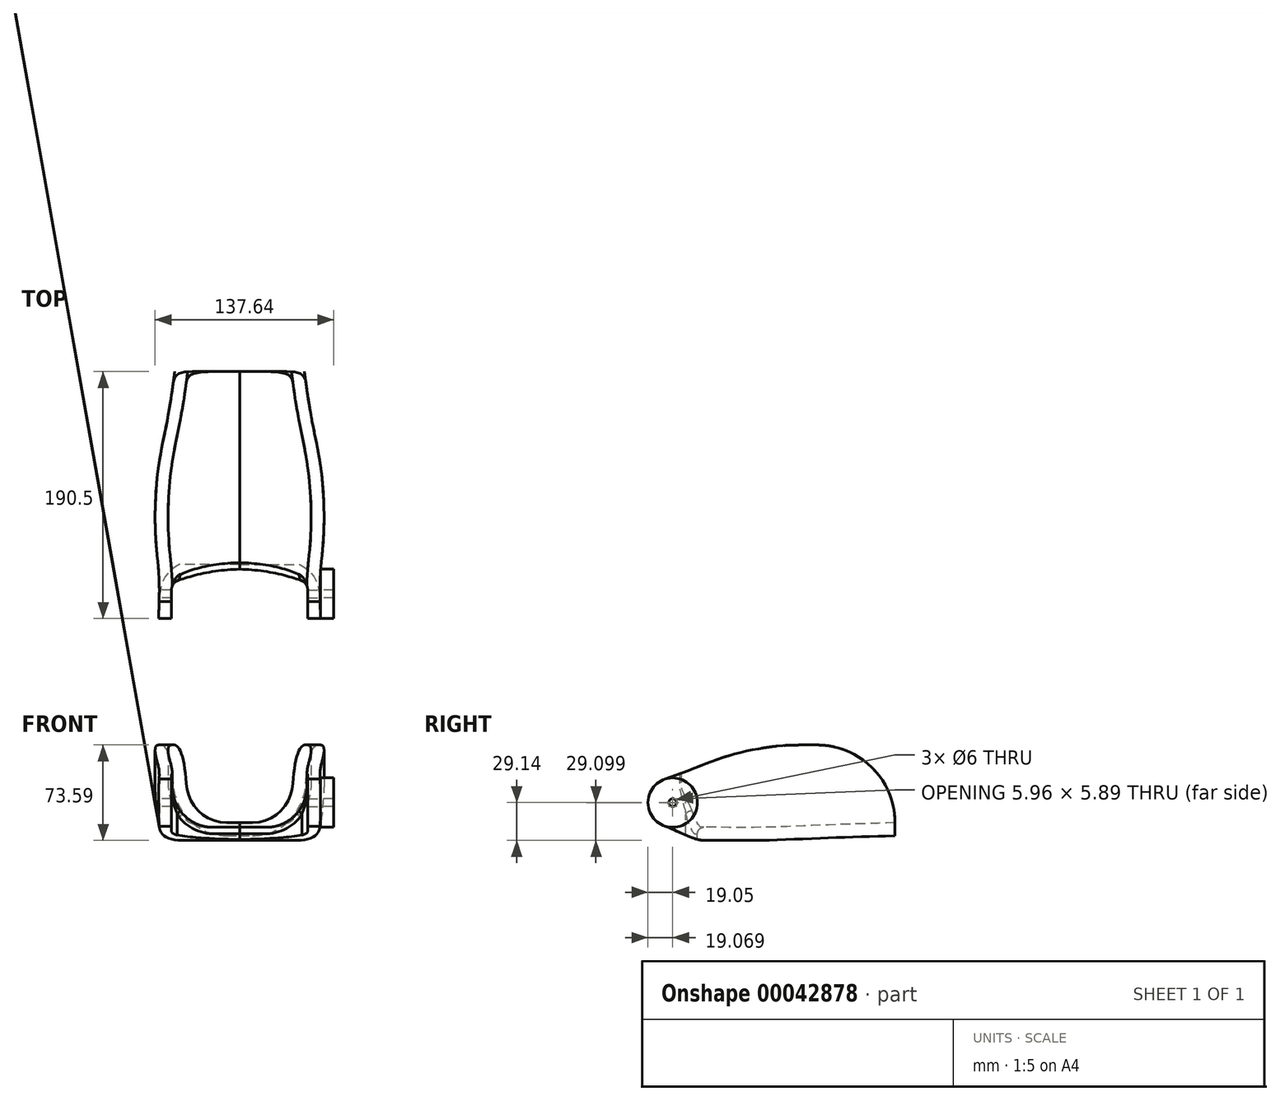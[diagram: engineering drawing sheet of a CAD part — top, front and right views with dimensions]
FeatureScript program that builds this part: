
annotation { "Feature Type Name" : "Feature", "Feature Type Description" : "" }
export const myFeature = defineFeature(function(context is Context, id is Id, definition is map)
    precondition{}
    {
        {
            assignVariable(context, id + "F0", {"name" : "FST", "anyValue" : 10 * mm});
        }
        {
            assignVariable(context, id + "F1", {"name" : "FSG", "anyValue" : 5 * mm});
        }
        {
            var Q0;
            Q0=qCreatedBy(makeId("Right.planeOp"),FACE);
            cPlane(context, id + "F2", {"entities" : qUnion([Q0]), "cplaneType" : CPlaneType.OFFSET, "offset" : (115 * mm / 2) + getVariable(context, 'FSG'), "width" : 150 * mm, "height" : 150 * mm});
        }
        {
            var Q0;
            Q0=qCreatedBy(makeId("Front.planeOp"),FACE);
            cPlane(context, id + "F3", {"entities" : qUnion([Q0]), "cplaneType" : CPlaneType.OFFSET, "offset" : 114.3 * mm, "width" : 150 * mm, "height" : 150 * mm});
        }
        {
            var Q0;
            Q0=qCreatedBy(makeId("Front.planeOp"),FACE);
            cPlane(context, id + "F4", {"entities" : qUnion([Q0]), "cplaneType" : CPlaneType.OFFSET, "offset" : 76.2 * mm, "width" : 150 * mm, "height" : 150 * mm});
        }
        {
            var Q0;
            Q0=qCreatedBy(makeId("Front.planeOp"),FACE);
            cPlane(context, id + "F5", {"entities" : qUnion([Q0]), "cplaneType" : CPlaneType.OFFSET, "offset" : (76.2 * mm) - 15 * mm, "width" : 150 * mm, "height" : 150 * mm});
        }
        {
            var Q0;
            Q0=qCreatedBy(makeId("Front.planeOp"),FACE);
            cPlane(context, id + "F6", {"entities" : qUnion([Q0]), "cplaneType" : CPlaneType.OFFSET, "offset" : (76.2 * mm) - 49 * mm, "width" : 150 * mm, "height" : 150 * mm});
        }
        {
            var Q0;
            Q0=qCreatedBy(makeId("Top.planeOp"),FACE);
            cPlane(context, id + "F7", {"entities" : qUnion([Q0]), "cplaneType" : CPlaneType.OFFSET, "offset" : 63.5 * mm + 10 * mm, "oppositeDirection" : true, "width" : 150 * mm, "height" : 150 * mm});
        }
        {
            var Q0;
            Q0=qCreatedBy(makeId("Front.planeOp"),FACE);
            cPlane(context, id + "F8", {"entities" : qUnion([Q0]), "cplaneType" : CPlaneType.OFFSET, "offset" : 76.2 * mm, "oppositeDirection" : true, "width" : 150 * mm, "height" : 150 * mm});
        }
        {
            var Q0;
            Q0=qCreatedBy(makeId("Front.planeOp"),FACE);
            cPlane(context, id + "F9", {"entities" : qUnion([Q0]), "cplaneType" : CPlaneType.OFFSET, "offset" : 76.2 * mm - 33.4 * mm, "oppositeDirection" : true, "width" : 150 * mm, "height" : 150 * mm});
        }
        {
            var Q0;
            Q0=qCreatedBy(makeId("Front.planeOp"),FACE);
            cPlane(context, id + "F10", {"entities" : qUnion([Q0]), "cplaneType" : CPlaneType.OFFSET, "offset" : 76.2 * mm - 73.4 * mm, "oppositeDirection" : true, "width" : 150 * mm, "height" : 150 * mm});
        }
        {
            var Q0;
            Q0=qCreatedBy(makeId("Top.planeOp"),FACE);
            var sketch = newSketch(context, id + "F11", { "sketchPlane" : qUnion([Q0])});
            skLineSegment(sketch, "E0", {"start": v(0, 76.2) * mm, "end": v(0, -76.2) * mm, "construction": true});
            skPoint(sketch, "E1", {"position": v(0, 0) * mm});
            skLineSegment(sketch, "E2", {"start": v(0, -76.2) * mm, "end": v(52.5, -76.2) * mm, "construction": true});
            skLineSegment(sketch, "E3", {"start": v(0, -61.2) * mm, "end": v(54, -61.2) * mm, "construction": true});
            skLineSegment(sketch, "E4", {"start": v(0, -27.2) * mm, "end": v(55, -27.2) * mm, "construction": true});
            skLineSegment(sketch, "E5", {"start": v(0, 2.8) * mm, "end": v(52.5, 2.8) * mm, "construction": true});
            skLineSegment(sketch, "E6", {"start": v(0, 42.8) * mm, "end": v(45, 42.8) * mm, "construction": true});
            skLineSegment(sketch, "E7", {"start": v(0, 76.2) * mm, "end": v(40, 76.2) * mm, "construction": true});
            skLineSegment(sketch, "E8.bottom", {"start": v(-157.02, 34.24) * mm, "end": v(-106.22, 34.24) * mm});
            skLineSegment(sketch, "E8.top", {"start": v(-157.02, -16.56) * mm, "end": v(-106.22, -16.56) * mm});
            skLineSegment(sketch, "E8.left", {"start": v(-157.02, 34.24) * mm, "end": v(-157.02, -16.56) * mm});
            skLineSegment(sketch, "E8.right", {"start": v(-106.22, 34.24) * mm, "end": v(-106.22, -16.56) * mm});
            skLineSegment(sketch, "E9", {"start": v(55, 76.2) * mm, "end": v(55, -76.2) * mm, "construction": true});
            skPoint(sketch, "E10", {"position": v(20, 76.2) * mm});
            skLineSegment(sketch, "E11", {"start": v(-60, 76.2) * mm, "end": v(-60, -76.2) * mm, "construction": true});
            skLineSegment(sketch, "E12", {"start": v(0, -95.25) * mm, "end": v(57.5, -95.25) * mm, "construction": true});
            skLineSegment(sketch, "E13", {"start": v(0, -114.3) * mm, "end": v(57.5, -114.3) * mm, "construction": true});
            skLineSegment(sketch, "E14", {"start": v(0, -84.2) * mm, "end": v(57.5, -84.2) * mm, "construction": true});
            skPoint(sketch, "E15.visualSharp", {"position": v(57.5, -84.2) * mm});
            skLineSegment(sketch, "E15.filletArc", {"start": v(57.5, -84.2) * mm, "end": v(57.5, -84.2) * mm});
            skLineSegment(sketch, "E16", {"start": v(40, 76.2) * mm, "end": v(50, 76.2) * mm});
            skLineSegment(sketch, "E17", {"start": v(45, 42.8) * mm, "end": v(55, 42.8) * mm, "construction": true});
            skLineSegment(sketch, "E18", {"start": v(52.5, 2.8) * mm, "end": v(62.5, 2.8) * mm, "construction": true});
            skLineSegment(sketch, "E19", {"start": v(55, -27.2) * mm, "end": v(65, -27.2) * mm, "construction": true});
            skLineSegment(sketch, "E20", {"start": v(54, -61.2) * mm, "end": v(64, -61.2) * mm, "construction": true});
            skLineSegment(sketch, "E21", {"start": v(52.5, -76.2) * mm, "end": v(62.5, -76.2) * mm, "construction": true});
            skLineSegment(sketch, "E22", {"start": v(57.5, -84.2) * mm, "end": v(67.5, -84.2) * mm});
            skLineSegment(sketch, "E23", {"start": v(57.5, -95.25) * mm, "end": v(67.5, -95.25) * mm});
            skLineSegment(sketch, "E24", {"start": v(57.5, -114.3) * mm, "end": v(67.5, -114.3) * mm});
            skFitSpline(sketch, "E25", {"points": [v(50, 76.2) * mm, v(55, 42.8) * mm, v(62.5, 2.8) * mm, v(65, -27.2) * mm, v(64, -61.2) * mm, v(62.5, -76.2) * mm, v(67.5, -84.2) * mm, v(67.5, -95.25) * mm, v(67.5, -114.3) * mm], "startDerivative": vector(28.82, -213.97) * mm, "endDerivative": vector(-0.1, -161.58) * mm});
            skLineSegment(sketch, "E26", {"start": v(55, -76.2) * mm, "end": v(55, -137.07) * mm, "construction": true});
            skFitSpline(sketch, "E27", {"points": [v(40, 76.2) * mm, v(45, 42.8) * mm, v(52.5, 2.8) * mm, v(55, -27.2) * mm, v(54, -61.2) * mm, v(52.5, -76.2) * mm, v(57.5, -84.2) * mm, v(57.5, -95.25) * mm, v(57.5, -114.3) * mm], "startDerivative": vector(29.26, -219.54) * mm, "endDerivative": vector(0.26, -174.77) * mm});
            skLineSegment(sketch, "E28", {"start": v(0, -114.05) * mm, "end": v(57.5, -114.05) * mm, "construction": true});
            skLineSegment(sketch, "E29", {"start": v(57.5, -114.05) * mm, "end": v(67.5, -114.05) * mm});
            skSolve(sketch);
        }
        {
            var Q0;
            Q0=qCreatedBy(id+"F3.planeOp",FACE);
            var sketch = newSketch(context, id + "F12", { "sketchPlane" : qUnion([Q0])});
            skLineSegment(sketch, "E30", {"start": v(0, 0) * mm, "end": v(52.5, 0) * mm, "construction": true});
            skLineSegment(sketch, "E31", {"start": v(52.5, 0) * mm, "end": v(62.5, 0) * mm});
            skLineSegment(sketch, "E32", {"start": v(0, 0) * mm, "end": v(0, -63.5) * mm, "construction": true});
            skLineSegment(sketch, "E33", {"start": v(0, 0) * mm, "end": v(47.5, 0) * mm, "construction": true});
            skLineSegment(sketch, "E34", {"start": v(52.5, 0) * mm, "end": v(52.5, -31.5) * mm});
            skLineSegment(sketch, "E35", {"start": v(20.5, -63.5) * mm, "end": v(0, -63.5) * mm});
            skLineSegment(sketch, "E36", {"start": v(0, -63.5) * mm, "end": v(0, -73.5) * mm});
            skArc(sketch, "E37.filletArc", {"start": v(20.5, -63.5) * mm, "mid": v(43.13, -54.13) * mm, "end": v(52.5, -31.5) * mm});
            skPoint(sketch, "E38", {"position": v(0, -35.5) * mm});
            skLineSegment(sketch, "E39", {"start": v(0, -35.5) * mm, "end": v(67.5, -35.5) * mm, "construction": true});
            skLineSegment(sketch, "E40", {"start": v(62.5, 0) * mm, "end": v(62.5, -58.5) * mm});
            skLineSegment(sketch, "E41", {"start": v(47.5, -73.5) * mm, "end": v(0, -73.5) * mm});
            skPoint(sketch, "E42.visualSharp", {"position": v(62.5, -73.5) * mm});
            skArc(sketch, "E42.filletArc", {"start": v(47.5, -73.5) * mm, "mid": v(58.1, -69.1) * mm, "end": v(62.5, -58.5) * mm});
            skSolve(sketch);
        }
        {
            var Q0;
            Q0=qCreatedBy(id+"F4.planeOp",FACE);
            var sketch = newSketch(context, id + "F13", { "sketchPlane" : qUnion([Q0])});
            skLineSegment(sketch, "E43", {"start": v(0, 0) * mm, "end": v(52.5, 0) * mm, "construction": true});
            skLineSegment(sketch, "E44", {"start": v(0, 0) * mm, "end": v(0, -63.5) * mm, "construction": true});
            skLineSegment(sketch, "E45", {"start": v(52.5, 0) * mm, "end": v(62.5, 0) * mm});
            skLineSegment(sketch, "E46", {"start": v(0, -63.5) * mm, "end": v(0, -73.5) * mm});
            skLineSegment(sketch, "E47", {"start": v(52.5, 0) * mm, "end": v(52.5, -31.5) * mm});
            skLineSegment(sketch, "E48", {"start": v(20.5, -63.5) * mm, "end": v(0, -63.5) * mm});
            skLineSegment(sketch, "E49", {"start": v(62.5, -58.5) * mm, "end": v(62.5, 0) * mm});
            skPoint(sketch, "E50.visualSharp", {"position": v(52.5, -63.5) * mm});
            skArc(sketch, "E50.filletArc", {"start": v(20.5, -63.5) * mm, "mid": v(43.13, -54.13) * mm, "end": v(52.5, -31.5) * mm});
            skLineSegment(sketch, "E51", {"start": v(47.5, -73.5) * mm, "end": v(0, -73.5) * mm});
            skPoint(sketch, "E52.visualSharp", {"position": v(62.5, -73.5) * mm});
            skArc(sketch, "E52.filletArc", {"start": v(47.5, -73.5) * mm, "mid": v(58.1, -69.1) * mm, "end": v(62.5, -58.5) * mm});
            skSolve(sketch);
        }
        {
            var Q0;
            Q0=qCreatedBy(id+"F5.planeOp",FACE);
            var sketch = newSketch(context, id + "F14", { "sketchPlane" : qUnion([Q0])});
            skLineSegment(sketch, "E53", {"start": v(0, 0) * mm, "end": v(54, 0) * mm, "construction": true});
            skLineSegment(sketch, "E54", {"start": v(0, 0) * mm, "end": v(0, -63.5) * mm, "construction": true});
            skLineSegment(sketch, "E55", {"start": v(54, 0) * mm, "end": v(64, 0) * mm});
            skLineSegment(sketch, "E56", {"start": v(0, -63.5) * mm, "end": v(0, -73.5) * mm});
            skLineSegment(sketch, "E57", {"start": v(54, 0) * mm, "end": v(54, -31.5) * mm});
            skLineSegment(sketch, "E58", {"start": v(22, -63.5) * mm, "end": v(0, -63.5) * mm});
            skLineSegment(sketch, "E59", {"start": v(64, 0) * mm, "end": v(64, -48.5) * mm});
            skLineSegment(sketch, "E60", {"start": v(39, -73.5) * mm, "end": v(0, -73.5) * mm});
            skPoint(sketch, "E61.visualSharp", {"position": v(54, -63.5) * mm});
            skArc(sketch, "E61.filletArc", {"start": v(22, -63.5) * mm, "mid": v(44.63, -54.13) * mm, "end": v(54, -31.5) * mm});
            skPoint(sketch, "E62.visualSharp", {"position": v(64, -73.5) * mm});
            skArc(sketch, "E62.filletArc", {"start": v(39, -73.5) * mm, "mid": v(56.68, -66.18) * mm, "end": v(64, -48.5) * mm});
            skSolve(sketch);
        }
        {
            var Q0;
            Q0=qCreatedBy(id+"F6.planeOp",FACE);
            var sketch = newSketch(context, id + "F15", { "sketchPlane" : qUnion([Q0])});
            skLineSegment(sketch, "E63", {"start": v(0, 0) * mm, "end": v(55, 0) * mm, "construction": true});
            skLineSegment(sketch, "E64", {"start": v(0, 0) * mm, "end": v(0, -63.5) * mm, "construction": true});
            skLineSegment(sketch, "E65", {"start": v(55, 0) * mm, "end": v(65, 0) * mm});
            skLineSegment(sketch, "E66", {"start": v(0, -63.5) * mm, "end": v(0, -73.5) * mm});
            skLineSegment(sketch, "E67", {"start": v(55, 0) * mm, "end": v(55, -31.5) * mm});
            skLineSegment(sketch, "E68", {"start": v(23, -63.5) * mm, "end": v(0, -63.5) * mm});
            skLineSegment(sketch, "E69", {"start": v(65, 0) * mm, "end": v(65, -31.5) * mm});
            skLineSegment(sketch, "E70", {"start": v(23, -73.5) * mm, "end": v(0, -73.5) * mm});
            skPoint(sketch, "E71.visualSharp", {"position": v(55, -63.5) * mm});
            skArc(sketch, "E71.filletArc", {"start": v(23, -63.5) * mm, "mid": v(45.63, -54.13) * mm, "end": v(55, -31.5) * mm});
            skPoint(sketch, "E72.visualSharp", {"position": v(65, -73.5) * mm});
            skArc(sketch, "E72.filletArc", {"start": v(23, -73.5) * mm, "mid": v(52.7, -61.2) * mm, "end": v(65, -31.5) * mm});
            skSolve(sketch);
        }
        {
            var Q0;
            Q0=qCreatedBy(id+"F8.planeOp",FACE);
            var sketch = newSketch(context, id + "F16", { "sketchPlane" : qUnion([Q0])});
            skLineSegment(sketch, "E73", {"start": v(0, 0) * mm, "end": v(0, -60) * mm, "construction": true});
            skLineSegment(sketch, "E74", {"start": v(0, 0) * mm, "end": v(40, 0) * mm, "construction": true});
            skLineSegment(sketch, "E75", {"start": v(0, -60) * mm, "end": v(10, -60) * mm});
            skLineSegment(sketch, "E76", {"start": v(40, 0) * mm, "end": v(50, 0) * mm});
            skLineSegment(sketch, "E77", {"start": v(0, -60) * mm, "end": v(0, -70) * mm});
            skLineSegment(sketch, "E78", {"start": v(0, -70) * mm, "end": v(10, -70) * mm});
            skLineSegment(sketch, "E79", {"start": v(50, -30) * mm, "end": v(50, 0) * mm});
            skLineSegment(sketch, "E80", {"start": v(40, -30) * mm, "end": v(40, 0) * mm});
            skPoint(sketch, "E81.visualSharp", {"position": v(40, -60) * mm});
            skArc(sketch, "E81.filletArc", {"start": v(10, -60) * mm, "mid": v(31.21, -51.21) * mm, "end": v(40, -30) * mm});
            skPoint(sketch, "E82.visualSharp", {"position": v(50, -70) * mm});
            skArc(sketch, "E82.filletArc", {"start": v(10, -70) * mm, "mid": v(38.28, -58.28) * mm, "end": v(50, -30) * mm});
            skSolve(sketch);
        }
        {
            var Q0;
            Q0=qCreatedBy(id+"F9.planeOp",FACE);
            var sketch = newSketch(context, id + "F17", { "sketchPlane" : qUnion([Q0])});
            skLineSegment(sketch, "E83", {"start": v(0, 0) * mm, "end": v(45, 0) * mm, "construction": true});
            skLineSegment(sketch, "E84", {"start": v(0, 0) * mm, "end": v(0, -61) * mm, "construction": true});
            skLineSegment(sketch, "E85", {"start": v(45, 0) * mm, "end": v(55, 0) * mm});
            skLineSegment(sketch, "E86", {"start": v(0, -61) * mm, "end": v(0, -71) * mm});
            skLineSegment(sketch, "E87", {"start": v(45, 0) * mm, "end": v(45, -31) * mm});
            skLineSegment(sketch, "E88", {"start": v(15, -61) * mm, "end": v(0, -61) * mm});
            skLineSegment(sketch, "E89", {"start": v(55, 0) * mm, "end": v(55, -31) * mm});
            skLineSegment(sketch, "E90", {"start": v(15, -71) * mm, "end": v(0, -71) * mm});
            skPoint(sketch, "E91.visualSharp", {"position": v(45, -61) * mm});
            skArc(sketch, "E91.filletArc", {"start": v(15, -61) * mm, "mid": v(36.21, -52.21) * mm, "end": v(45, -31) * mm});
            skPoint(sketch, "E92.visualSharp", {"position": v(55, -71) * mm});
            skArc(sketch, "E92.filletArc", {"start": v(15, -71) * mm, "mid": v(43.28, -59.28) * mm, "end": v(55, -31) * mm});
            skSolve(sketch);
        }
        {
            var Q0;
            Q0=qCreatedBy(id+"F10.planeOp",FACE);
            var sketch = newSketch(context, id + "F18", { "sketchPlane" : qUnion([Q0])});
            skLineSegment(sketch, "E93", {"start": v(0, 0) * mm, "end": v(52.5, 0) * mm, "construction": true});
            skLineSegment(sketch, "E94", {"start": v(0, 0) * mm, "end": v(0, -62.5) * mm, "construction": true});
            skLineSegment(sketch, "E95", {"start": v(52.5, 0) * mm, "end": v(62.5, 0) * mm});
            skLineSegment(sketch, "E96", {"start": v(0, -62.5) * mm, "end": v(0, -72.5) * mm});
            skLineSegment(sketch, "E97", {"start": v(52.5, 0) * mm, "end": v(52.5, -31.5) * mm});
            skLineSegment(sketch, "E98", {"start": v(21.5, -62.5) * mm, "end": v(0, -62.5) * mm});
            skLineSegment(sketch, "E99", {"start": v(62.5, 0) * mm, "end": v(62.5, -31.5) * mm});
            skLineSegment(sketch, "E100", {"start": v(21.5, -72.5) * mm, "end": v(0, -72.5) * mm});
            skPoint(sketch, "E101.visualSharp", {"position": v(52.5, -62.5) * mm});
            skArc(sketch, "E101.filletArc", {"start": v(21.5, -62.5) * mm, "mid": v(43.42, -53.42) * mm, "end": v(52.5, -31.5) * mm});
            skPoint(sketch, "E102.visualSharp", {"position": v(62.5, -72.5) * mm});
            skArc(sketch, "E102.filletArc", {"start": v(21.5, -72.5) * mm, "mid": v(50.5, -60.5) * mm, "end": v(62.5, -31.5) * mm});
            skSolve(sketch);
        }
        {
            var Q0;
            Q0=qCreatedBy(makeId("Right.planeOp"),FACE);
            var sketch = newSketch(context, id + "F19", { "sketchPlane" : qUnion([Q0])});
            skLineSegment(sketch, "E103", {"start": v(-76.2, 0) * mm, "end": v(76.2, 0) * mm, "construction": true});
            skLineSegment(sketch, "E104", {"start": v(76.2, 0) * mm, "end": v(76.2, -60) * mm, "construction": true});
            skLineSegment(sketch, "E105", {"start": v(42.8, 0) * mm, "end": v(42.8, -61) * mm, "construction": true});
            skLineSegment(sketch, "E106", {"start": v(2.8, 0) * mm, "end": v(2.8, -62.5) * mm, "construction": true});
            skLineSegment(sketch, "E107", {"start": v(-27.2, 0) * mm, "end": v(-27.2, -63.5) * mm, "construction": true});
            skLineSegment(sketch, "E108", {"start": v(-61.2, 0) * mm, "end": v(-61.2, -63.5) * mm, "construction": true});
            skLineSegment(sketch, "E109", {"start": v(-76.2, 0) * mm, "end": v(-76.2, -63.5) * mm, "construction": true});
            skPoint(sketch, "E110", {"position": v(0, 0) * mm});
            skLineSegment(sketch, "E111", {"start": v(76.2, -60) * mm, "end": v(76.2, -70) * mm});
            skLineSegment(sketch, "E112", {"start": v(42.8, -61) * mm, "end": v(42.8, -71) * mm});
            skLineSegment(sketch, "E113", {"start": v(2.8, -62.5) * mm, "end": v(2.8, -72.5) * mm});
            skLineSegment(sketch, "E114", {"start": v(-27.2, -63.5) * mm, "end": v(-27.2, -73.5) * mm});
            skLineSegment(sketch, "E115", {"start": v(-61.2, -63.5) * mm, "end": v(-61.2, -73.5) * mm});
            skLineSegment(sketch, "E116", {"start": v(-76.2, -63.5) * mm, "end": v(-76.2, -73.5) * mm});
            skLineSegment(sketch, "E117", {"start": v(-84.2, 0) * mm, "end": v(-84.2, -63.5) * mm, "construction": true});
            skLineSegment(sketch, "E118", {"start": v(-84.2, -63.5) * mm, "end": v(-84.2, -73.5) * mm});
            skLineSegment(sketch, "E119", {"start": v(-95.25, 0) * mm, "end": v(-95.25, -63.5) * mm, "construction": true});
            skLineSegment(sketch, "E120", {"start": v(-114.3, 0) * mm, "end": v(-114.3, -63.5) * mm, "construction": true});
            skLineSegment(sketch, "E121", {"start": v(-95.25, -63.5) * mm, "end": v(-95.25, -73.5) * mm});
            skLineSegment(sketch, "E122", {"start": v(-114.3, -63.5) * mm, "end": v(-114.3, -73.5) * mm});
            skFitSpline(sketch, "E123", {"points": [v(76.2, -60) * mm, v(42.8, -61) * mm, v(2.8, -62.5) * mm, v(-27.2, -63.5) * mm, v(-61.2, -63.5) * mm, v(-76.2, -63.5) * mm, v(-84.2, -63.5) * mm, v(-95.25, -63.5) * mm, v(-114.3, -63.5) * mm], "startDerivative": vector(-217.44, -6.1) * mm, "endDerivative": vector(-173.87, 0) * mm});
            skFitSpline(sketch, "E124", {"points": [v(76.2, -70) * mm, v(42.8, -71) * mm, v(2.8, -72.5) * mm, v(-27.2, -73.5) * mm, v(-61.2, -73.5) * mm, v(-76.2, -73.5) * mm, v(-84.2, -73.5) * mm, v(-95.25, -73.5) * mm, v(-114.3, -73.5) * mm], "startDerivative": vector(-217.36, -6.1) * mm, "endDerivative": vector(-173.09, 0) * mm});
            skLineSegment(sketch, "E125.bottom", {"start": v(-173.81, 0) * mm, "end": v(-223.81, 0) * mm, "construction": true});
            skLineSegment(sketch, "E125.top", {"start": v(-173.81, -50) * mm, "end": v(-223.81, -50) * mm, "construction": true});
            skLineSegment(sketch, "E125.left", {"start": v(-173.81, 0) * mm, "end": v(-173.81, -50) * mm, "construction": true});
            skLineSegment(sketch, "E125.right", {"start": v(-223.81, 0) * mm, "end": v(-223.81, -50) * mm, "construction": true});
            skSolve(sketch);
        }
        {
            var Q0;
            Q0=makeQuery(id+"F16.imprint","IMPRINT",FACE,{"disambiguationData":[TD([[makeQuery(id+"F16.imprint","IMPRINT",EDGE,{"derivedFrom":sQuery(id+"F16.wireOp",EDGE,"E75")}),-1.0]])]});
            var Q1;
            Q1=makeQuery(id+"F17.imprint","IMPRINT",FACE,{"disambiguationData":[TD([[makeQuery(id+"F17.imprint","IMPRINT",EDGE,{"derivedFrom":sQuery(id+"F17.wireOp",EDGE,"E85")}),-1.0]])]});
            var Q2;
            Q2=makeQuery(id+"F18.imprint","IMPRINT",FACE,{"disambiguationData":[TD([[makeQuery(id+"F18.imprint","IMPRINT",EDGE,{"derivedFrom":sQuery(id+"F18.wireOp",EDGE,"E95")}),-1.0]])]});
            var Q3;
            Q3=makeQuery(id+"F15.imprint","IMPRINT",FACE,{"disambiguationData":[TD([[makeQuery(id+"F15.imprint","IMPRINT",EDGE,{"derivedFrom":sQuery(id+"F15.wireOp",EDGE,"E65")}),-1.0]])]});
            var Q4;
            Q4=makeQuery(id+"F14.imprint","IMPRINT",FACE,{"disambiguationData":[TD([[makeQuery(id+"F14.imprint","IMPRINT",EDGE,{"derivedFrom":sQuery(id+"F14.wireOp",EDGE,"E55")}),-1.0]])]});
            var Q5;
            Q5=makeQuery(id+"F13.imprint","IMPRINT",FACE,{"disambiguationData":[TD([[makeQuery(id+"F13.imprint","IMPRINT",EDGE,{"derivedFrom":sQuery(id+"F13.wireOp",EDGE,"E45")}),-1.0]])]});
            var Q6;
            Q6=makeQuery(id+"F12.imprint","IMPRINT",FACE,{"disambiguationData":[TD([[makeQuery(id+"F12.imprint","IMPRINT",EDGE,{"derivedFrom":sQuery(id+"F12.wireOp",EDGE,"E31")}),-1.0]])]});
            loft(context, id + "F20", {"sheetProfilesArray" : [{ "sheetProfileEntities" : qUnion([Q0]) }, { "sheetProfileEntities" : qUnion([Q1]) }, { "sheetProfileEntities" : qUnion([Q2]) }, { "sheetProfileEntities" : qUnion([Q3]) }, { "sheetProfileEntities" : qUnion([Q4]) }, { "sheetProfileEntities" : qUnion([Q5]) }, { "sheetProfileEntities" : qUnion([Q6]) }]});
        }
        {
            var Q0;
            Q0=makeQuery(id+"F20.opLoft","MID_CAP_EDGE",EDGE,{"disambiguationData":[OSD([sQuery(id+"F16.wireOp",EDGE,"E76"),sQuery(id+"F16.wireOp",EDGE,"E79"),sQuery(id+"F16.wireOp",EDGE,"E80")])],"capPos":0.0});
            fillet(context, id + "F21", {"entities" : qUnion([Q0]), "radius" : 60 * mm, "tangentPropagation" : true, "allowEdgeOverflow" : false});
        }
        {
            var Q0;
            Q0=qCreatedBy(id+"F2.planeOp",FACE);
            var sketch = newSketch(context, id + "F22", { "sketchPlane" : qUnion([Q0])});
            skCircle(sketch, "E126", {"center": v(-95.25, -44.45) * mm, "radius": 19.05 * mm});
            skLineSegment(sketch, "E127", {"start": v(-76.2, 0) * mm, "end": v(76.2, 0) * mm, "construction": true});
            skLineSegment(sketch, "E128", {"start": v(-76.2, 0) * mm, "end": v(-76.2, -63.5) * mm, "construction": true});
            skLineSegment(sketch, "E129", {"start": v(-76.2, -63.5) * mm, "end": v(-76.2, -73.5) * mm, "construction": true});
            skLineSegment(sketch, "E130", {"start": v(-76.2, -73.5) * mm, "end": v(-114.3, -73.5) * mm, "construction": true});
            skLineSegment(sketch, "E131", {"start": v(-76.2, -25.4) * mm, "end": v(-114.3, -25.4) * mm, "construction": true});
            skLineSegment(sketch, "E132", {"start": v(-76.2, 0) * mm, "end": v(-114.3, 0) * mm, "construction": true});
            skLineSegment(sketch, "E133", {"start": v(-95.25, -44.45) * mm, "end": v(-114.3, -44.45) * mm, "construction": true});
            skLineSegment(sketch, "E134", {"start": v(-95.25, -44.45) * mm, "end": v(-95.25, -73.5) * mm, "construction": true});
            skLineSegment(sketch, "E135", {"start": v(-127.04, -54.43) * mm, "end": v(-127.04, -88.5) * mm});
            skLineSegment(sketch, "E136", {"start": v(-127.04, -54.43) * mm, "end": v(-127.04, 0) * mm});
            skLineSegment(sketch, "E137", {"start": v(-127.04, 0) * mm, "end": v(0, 0) * mm, "construction": true});
            skLineSegment(sketch, "E138", {"start": v(-51.2, 0) * mm, "end": v(-51.2, -8) * mm, "construction": true});
            skPoint(sketch, "E139", {"position": v(-76.2, -17) * mm});
            skLineSegment(sketch, "E140", {"start": v(-16.2, 0) * mm, "end": v(-16.2, -1) * mm, "construction": true});
            skLineSegment(sketch, "E141", {"start": v(3.8, 0) * mm, "end": v(3.8, 0) * mm});
            skPoint(sketch, "E142", {"position": v(13.8, 0) * mm});
            skLineSegment(sketch, "E143", {"start": v(-127.04, 0) * mm, "end": v(-127.04, 22.7) * mm});
            skLineSegment(sketch, "E144", {"start": v(-127.04, 22.7) * mm, "end": v(13.8, 22.7) * mm});
            skLineSegment(sketch, "E145", {"start": v(13.8, 22.7) * mm, "end": v(13.8, 0) * mm});
            skCircle(sketch, "E146", {"center": v(-95.25, -44.45) * mm, "radius": 3 * mm});
            skLineSegment(sketch, "E147", {"start": v(-95.25, -44.45) * mm, "end": v(-101.14, -26.33) * mm, "construction": true});
            skLineSegment(sketch, "E148", {"start": v(-95.25, -44.45) * mm, "end": v(-95.25, -25.4) * mm, "construction": true});
            skFitSpline(sketch, "E149", {"points": [v(-101.14, -26.33) * mm, v(-76.2, -17) * mm, v(-51.2, -8) * mm, v(-16.2, -1) * mm, v(3.8, 0) * mm, v(13.8, 0) * mm], "startDerivative": vector(117.64, 43.18) * mm, "endDerivative": vector(70.79, -0.21) * mm});
            skLineSegment(sketch, "E150", {"start": v(-95.25, -44.45) * mm, "end": v(-103.3, -61.72) * mm, "construction": true});
            skLineSegment(sketch, "E151", {"start": v(-72.2, -63.5) * mm, "end": v(-72.2, -73.5) * mm, "construction": true});
            skFitSpline(sketch, "E152", {"points": [v(-72.2, -73.5) * mm, v(-103.3, -61.72) * mm], "startDerivative": vector(-18, 0) * mm, "endDerivative": vector(-31.1, 11.78) * mm});
            skLineSegment(sketch, "E153", {"start": v(-127.04, -88.5) * mm, "end": v(-72.2, -88.5) * mm});
            skLineSegment(sketch, "E154", {"start": v(-72.2, -88.5) * mm, "end": v(-72.2, -73.5) * mm});
            skSolve(sketch);
        }
        {
            var Q0;
            Q0=makeQuery(id+"F22.imprint","IMPRINT",FACE,{"disambiguationData":[TD([[makeQuery(id+"F22.imprint","IMPRINT",EDGE,{"derivedFrom":sQuery(id+"F22.wireOp",EDGE,"E135")}),1.0]])]});
            extrude(context, id + "F23", {"entities" : qUnion([Q0]), "operationType" : NewBodyOperationType.REMOVE, "endBound" : BoundingType.SYMMETRIC, "oppositeDirection" : true, "depth" : 140 * mm});
        }
        {
            var Q0;
            Q0=makeQuery(id+"F22.imprint","IMPRINT",FACE,{"disambiguationData":[TD([[makeQuery(id+"F22.imprint","IMPRINT",EDGE,{"derivedFrom":sQuery(id+"F22.wireOp",EDGE,"E146")}),1.0]])]});
            extrude(context, id + "F24", {"entities" : qUnion([Q0]), "operationType" : NewBodyOperationType.REMOVE, "endBound" : BoundingType.THROUGH_ALL, "oppositeDirection" : true, "depth" : 25 * mm});
        }
        {
            var Q0;
            Q0=qCreatedBy(id+"F7.planeOp",FACE);
            var sketch = newSketch(context, id + "F25", { "sketchPlane" : qUnion([Q0])});
            skLineSegment(sketch, "E155", {"start": v(0, 76.2) * mm, "end": v(0, -76.2) * mm});
            skLineSegment(sketch, "E156", {"start": v(0, -114.3) * mm, "end": v(52.5, -114.3) * mm});
            skLineSegment(sketch, "E157", {"start": v(0, -76.2) * mm, "end": v(0, -114.3) * mm, "construction": true});
            skLineSegment(sketch, "E158", {"start": v(0, -95.25) * mm, "end": v(52.5, -95.25) * mm, "construction": true});
            skLineSegment(sketch, "E159.rect.bottom", {"start": v(62.5, -98.25) * mm, "end": v(52.5, -98.25) * mm, "construction": true});
            skLineSegment(sketch, "E159.rect.top", {"start": v(62.5, -92.25) * mm, "end": v(52.5, -92.25) * mm, "construction": true});
            skLineSegment(sketch, "E159.rect.left", {"start": v(62.5, -98.25) * mm, "end": v(62.5, -92.25) * mm, "construction": true});
            skLineSegment(sketch, "E159.rect.right", {"start": v(52.5, -98.25) * mm, "end": v(52.5, -92.25) * mm, "construction": true});
            skPoint(sketch, "E159.rect.middle", {"position": v(57.5, -95.25) * mm});
            skLineSegment(sketch, "E160", {"start": v(52.5, -95.25) * mm, "end": v(52.5, -92.25) * mm, "construction": true});
            skLineSegment(sketch, "E161", {"start": v(0, -72.2) * mm, "end": v(-24.84, -72.2) * mm, "construction": true});
            skLineSegment(sketch, "E162", {"start": v(0, -72.2) * mm, "end": v(0, -114.3) * mm});
            skLineSegment(sketch, "E163", {"start": v(52.5, -114.3) * mm, "end": v(52.5, -92.25) * mm});
            skArc(sketch, "E164", {"start": v(52.5, -92.25) * mm, "mid": v(51.33, -88.09) * mm, "end": v(48.17, -85.14) * mm});
            skArc(sketch, "E165", {"start": v(48.17, -85.14) * mm, "mid": v(24.45, -78.7) * mm, "end": v(0, -76.2) * mm});
            skSolve(sketch);
        }
        {
            var Q0;
            {var subQ7=sQuery(id+"F25.wireOp",EDGE,"E156");Q0=makeQuery(id+"F25.imprint","IMPRINT",FACE,{"disambiguationData":[TD([[makeQuery(id+"F25.imprint","IMPRINT",EDGE,{"derivedFrom":subQ7}),1.0]])]});}
            var Q1;
            {var subQ0=sQuery(id+"F25.wireOp",EDGE,"6ab98432-ff88-4967-8b7e-415d656d9d2a");var subQ1=makeQuery(id+"F25.imprint","INTERSECT",VERTEX,{"derivedFrom":[subQ0,sQuery(id+"F25.wireOp",EDGE,"E163")]});Q1=makeQuery(id+"F25.imprint","IMPRINT",FACE,{"disambiguationData":[TD([[makeQuery(id+"F25.imprint","IMPRINT",EDGE,{"disambiguationData":[TD([[subQ1,-1.0]])],"derivedFrom":subQ0}),1.0]])]});}
            var Q2;
            {var subQ3=sQuery(id+"F25.wireOp",EDGE,"E162");var subQ6=makeQuery(id+"F25.imprint","IMPRINT",VERTEX,{"derivedFrom":subQ3});Q2=makeQuery(id+"F25.imprint","IMPRINT",FACE,{"disambiguationData":[TD([[makeQuery(id+"F25.imprint","IMPRINT",EDGE,{"disambiguationData":[TD([[subQ6,1.0]])],"derivedFrom":subQ3}),1.0]])]});}
            var Q3;
            {var subQ0=sQuery(id+"F25.wireOp",EDGE,"E162");var subQ1=sQuery(id+"F25.wireOp",EDGE,"4ed179fe-1dec-4f78-bcb3-8e963e810ee6");var subQ2=makeQuery(id+"F25.imprint","INTERSECT",VERTEX,{"disambiguationData":[OD(0.0)],"derivedFrom":[subQ1,subQ0]});Q3=makeQuery(id+"F25.imprint","IMPRINT",FACE,{"disambiguationData":[TD([[makeQuery(id+"F25.imprint","IMPRINT",EDGE,{"disambiguationData":[TD([[subQ2,1.0]])],"derivedFrom":subQ1}),1.0]])]});}
            extrude(context, id + "F26", {"entities" : qUnion([Q0, Q1, Q2, Q3]), "operationType" : NewBodyOperationType.REMOVE, "endBound" : BoundingType.SYMMETRIC, "oppositeDirection" : true, "depth" : 127 * mm});
        }
        {
            var Q0;
            Q0=makeQuery(id+"F26.boolean.opBoolean","INTERSECT",EDGE,{"derivedFrom":[makeQuery(id+"F20.opLoft","SWEPT_FACE",FACE,{"disambiguationData":[OSD([sQuery(id+"F16.wireOp",EDGE,"E76"),sQuery(id+"F16.wireOp",EDGE,"E80"),sQuery(id+"F16.wireOp",EDGE,"E81.filletArc"),sQuery(id+"F17.wireOp",EDGE,"E85"),sQuery(id+"F17.wireOp",EDGE,"E87"),sQuery(id+"F17.wireOp",EDGE,"E91.filletArc")])]}),makeQuery(id+"F26.opExtrude","SWEPT_FACE",FACE,{"disambiguationData":[OSD([sQuery(id+"F25.wireOp",EDGE,"E165")])]})]});
            var Q1;
            Q1=makeQuery(id+"F26.boolean.opBoolean","INTERSECT",EDGE,{"derivedFrom":[makeQuery(id+"F20.opLoft","SWEPT_FACE",FACE,{"disambiguationData":[OSD([sQuery(id+"F16.wireOp",EDGE,"E76"),sQuery(id+"F16.wireOp",EDGE,"E80"),sQuery(id+"F16.wireOp",EDGE,"E81.filletArc"),sQuery(id+"F17.wireOp",EDGE,"E85"),sQuery(id+"F17.wireOp",EDGE,"E87"),sQuery(id+"F17.wireOp",EDGE,"E91.filletArc")])]}),makeQuery(id+"F26.opExtrude","SWEPT_FACE",FACE,{"disambiguationData":[OSD([sQuery(id+"F25.wireOp",EDGE,"E164")])]})]});
            fillet(context, id + "F27", {"entities" : qUnion([Q0, Q1]), "radius" : 5 * mm, "tangentPropagation" : true, "allowEdgeOverflow" : false});
        }
        {
            var Q0;
            Q0=qCreatedBy(id+"F2.planeOp",FACE);
            var sketch = newSketch(context, id + "F28", { "sketchPlane" : qUnion([Q0])});
            skLineSegment(sketch, "E166", {"start": v(-76.2, 0) * mm, "end": v(76.2, 0) * mm, "construction": true});
            skLineSegment(sketch, "E167", {"start": v(-76.2, 0) * mm, "end": v(-76.2, -63.5) * mm, "construction": true});
            skLineSegment(sketch, "E168", {"start": v(-76.2, -63.5) * mm, "end": v(-114.3, -63.5) * mm, "construction": true});
            skCircle(sketch, "E169", {"center": v(-95.25, -44.45) * mm, "radius": 19.05 * mm});
            skCircle(sketch, "E170", {"center": v(-95.25, -44.45) * mm, "radius": 3 * mm});
            skSolve(sketch);
        }
        {
            var Q0;
            Q0=makeQuery(id+"F28.imprint","IMPRINT",FACE,{"disambiguationData":[TD([[makeQuery(id+"F28.imprint","IMPRINT",EDGE,{"derivedFrom":sQuery(id+"F28.wireOp",EDGE,"E169")}),1.0]])]});
            extrude(context, id + "F29", {"entities" : qUnion([Q0]), "depth" : getVariable(context, 'FST')});
        }
        {
            var Q0;
            Q0=makeQuery(id+"F20.opLoft","SWEPT_BODY",BODY,{"disambiguationData":[OSD([makeQuery(id+"F13.imprint","IMPRINT",FACE,{"disambiguationData":[TD([[makeQuery(id+"F13.imprint","IMPRINT",EDGE,{"derivedFrom":sQuery(id+"F13.wireOp",EDGE,"E45")}),-1.0]])]}),sQuery(id+"F14.wireOp",EDGE,"E55"),sQuery(id+"F15.wireOp",EDGE,"E65"),makeQuery(id+"F16.imprint","IMPRINT",FACE,{"disambiguationData":[TD([[makeQuery(id+"F16.imprint","IMPRINT",EDGE,{"derivedFrom":sQuery(id+"F16.wireOp",EDGE,"E75")}),-1.0]])]}),sQuery(id+"F17.wireOp",EDGE,"E85"),sQuery(id+"F18.wireOp",EDGE,"E95")])]});
            var Q1;
            Q1=qCreatedBy(makeId("Right.planeOp"),FACE);
            mirror(context, id + "F30", {"operationType" : NewBodyOperationType.ADD, "entities" : qUnion([Q0]), "mirrorPlane" : qUnion([Q1])});
        }
    });
